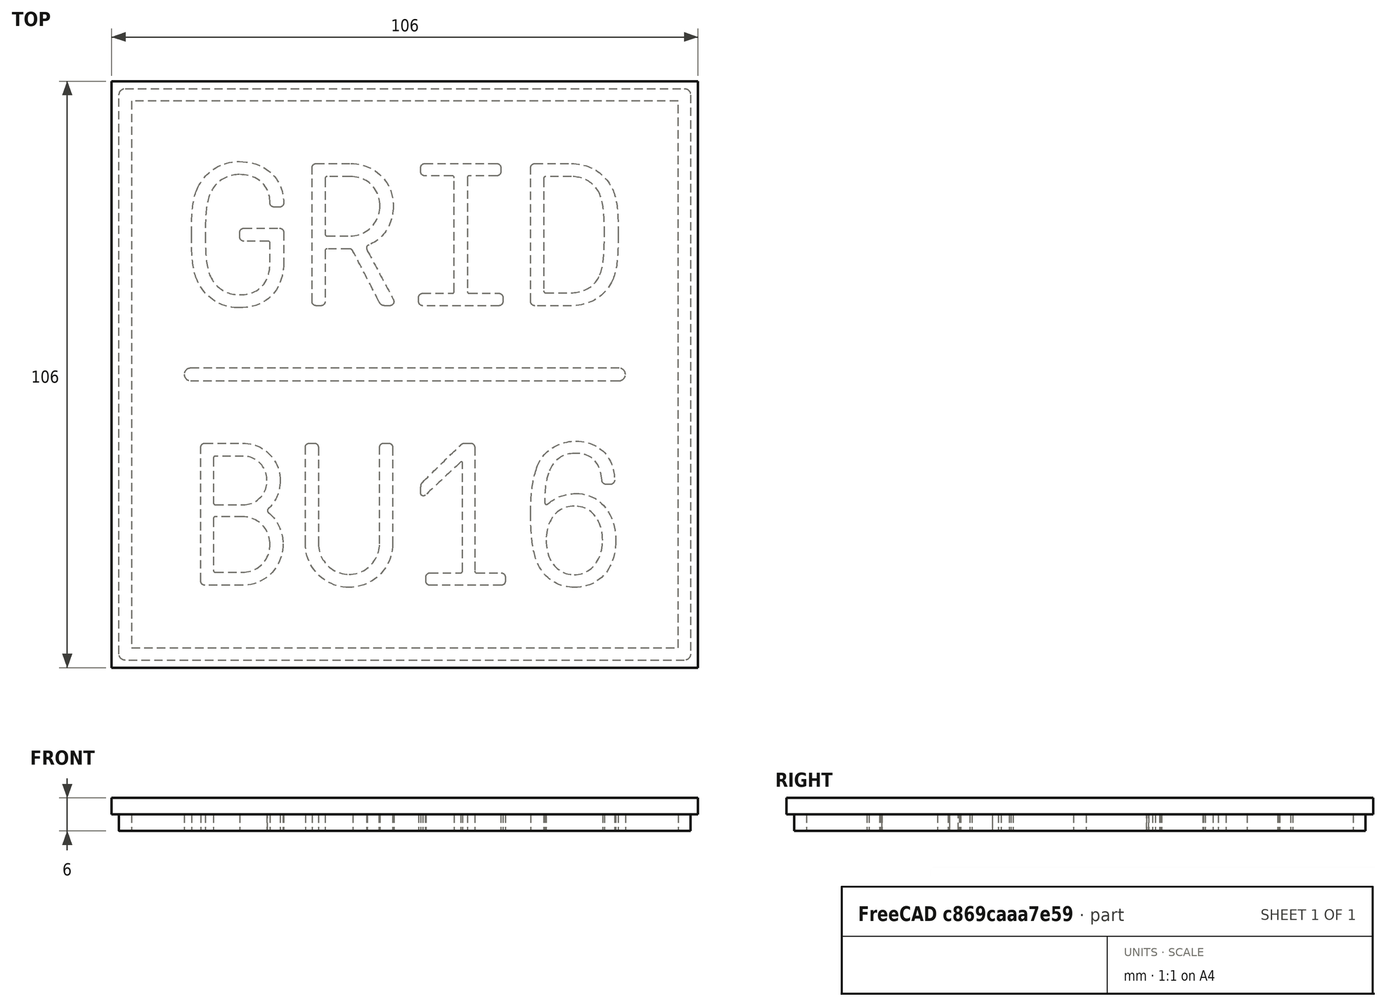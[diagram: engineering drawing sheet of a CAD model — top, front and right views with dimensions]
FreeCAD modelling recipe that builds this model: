
FCSTD DOCUMENT  (FreeCAD 0.18R16131 (Git))
Label: Grid-BU16
License: All rights reserved
LicenseURL: http://en.wikipedia.org/wiki/All_rights_reserved
objects: Sketcher::SketchObject×3, PartDesign::Pad×3, PartDesign::Body×1
note: 10 computed .brp shape members not serialized (recipe doc carries the construction recipe); baked Part::Feature solids carry a one-line shape summary decoded from their .brp

FEATURE [Sketcher::SketchObject] Sketch016
  Placement = pos=(-80,80,0) rot=(0,0,1;0rad)
  sketch-geometry (12):
    g0: BSplineCurve PolesCount=2 KnotsCount=2 Degree=1 IsPeriodic=0
    g1: BSplineCurve PolesCount=4 KnotsCount=2 Degree=3 IsPeriodic=0
    g2: BSplineCurve PolesCount=2 KnotsCount=2 Degree=1 IsPeriodic=0
    g3: BSplineCurve PolesCount=4 KnotsCount=2 Degree=3 IsPeriodic=0
    g4: BSplineCurve PolesCount=2 KnotsCount=2 Degree=1 IsPeriodic=0
    g5: BSplineCurve PolesCount=4 KnotsCount=2 Degree=3 IsPeriodic=0
    g6: BSplineCurve PolesCount=2 KnotsCount=2 Degree=1 IsPeriodic=0
    g7: BSplineCurve PolesCount=4 KnotsCount=2 Degree=3 IsPeriodic=0
    g8: BSplineCurve PolesCount=2 KnotsCount=2 Degree=1 IsPeriodic=0
    g9: BSplineCurve PolesCount=2 KnotsCount=2 Degree=1 IsPeriodic=0
    g10: BSplineCurve PolesCount=2 KnotsCount=2 Degree=1 IsPeriodic=0
    g11: BSplineCurve PolesCount=2 KnotsCount=2 Degree=1 IsPeriodic=0
  constraints (12):
    c: Coincident(g0,g1)
    c: Coincident(g1,g2)
    c: Coincident(g2,g3)
    c: Coincident(g3,g4)
    c: Coincident(g4,g5)
    c: Coincident(g5,g6)
    c: Coincident(g6,g7)
    c: Coincident(g7,g0)
    c: Coincident(g8,g9)
    c: Coincident(g9,g10)
    c: Coincident(g10,g11)
    c: Coincident(g11,g8)
FEATURE [Sketcher::SketchObject] Sketch017
  sketch-geometry (5):
    g0: LineSegment StartX=-53 StartY=53 StartZ=0 EndX=-53 EndY=-53 EndZ=0
    g1: LineSegment StartX=-53 StartY=-53 StartZ=0 EndX=53 EndY=-53 EndZ=0
    g2: LineSegment StartX=53 StartY=-53 StartZ=0 EndX=53 EndY=53 EndZ=0
    g3: LineSegment StartX=53 StartY=53 StartZ=0 EndX=-53 EndY=53 EndZ=0
    g4: Circle [constr] CenterX=0 CenterY=0 CenterZ=0 NormalX=0 NormalY=0 NormalZ=1 AngleXU=0 Radius=74.9533
  constraints (14):
    c: Coincident(g0,g1)
    c: Coincident(g1,g2)
    c: Coincident(g2,g3)
    c: Coincident(g3,g0)
    c: Equal(g0,g1)
    c: Equal(g0,g2)
    c: Equal(g0,g3)
    c: PointOnObject(g0,g4)
    c: PointOnObject(g1,g4)
    c: PointOnObject(g2,g4)
    c: PointOnObject(g3,g4)
    c: Horizontal(g3)
    c: Coincident(g4,g-1)
    c: DistanceX(g3,g3) = 106
FEATURE [PartDesign::Pad] Pad
  Length = 3
  Length2 = 100
  Profile = -> Sketch017
  Type = 0
FEATURE [Sketcher::SketchObject] Sketch018
  Placement = pos=(-80,80,0) rot=(0,0,1;0rad)
  sketch-geometry (178):
    g0: BSplineCurve PolesCount=4 KnotsCount=2 Degree=3 IsPeriodic=0
    g1: BSplineCurve PolesCount=4 KnotsCount=2 Degree=3 IsPeriodic=0
    g2: BSplineCurve PolesCount=4 KnotsCount=2 Degree=3 IsPeriodic=0
    g3: BSplineCurve PolesCount=4 KnotsCount=2 Degree=3 IsPeriodic=0
    g4: BSplineCurve PolesCount=2 KnotsCount=2 Degree=1 IsPeriodic=0
    g5: BSplineCurve PolesCount=4 KnotsCount=2 Degree=3 IsPeriodic=0
    g6: BSplineCurve PolesCount=2 KnotsCount=2 Degree=1 IsPeriodic=0
    g7: BSplineCurve PolesCount=4 KnotsCount=2 Degree=3 IsPeriodic=0
    g8: BSplineCurve PolesCount=4 KnotsCount=2 Degree=3 IsPeriodic=0
    g9: BSplineCurve PolesCount=4 KnotsCount=2 Degree=3 IsPeriodic=0
    g10: BSplineCurve PolesCount=4 KnotsCount=2 Degree=3 IsPeriodic=0
    g11: BSplineCurve PolesCount=2 KnotsCount=2 Degree=1 IsPeriodic=0
    g12: BSplineCurve PolesCount=4 KnotsCount=2 Degree=3 IsPeriodic=0
    g13: BSplineCurve PolesCount=4 KnotsCount=2 Degree=3 IsPeriodic=0
    g14: BSplineCurve PolesCount=2 KnotsCount=2 Degree=1 IsPeriodic=0
    g15: BSplineCurve PolesCount=4 KnotsCount=2 Degree=3 IsPeriodic=0
    g16: BSplineCurve PolesCount=2 KnotsCount=2 Degree=1 IsPeriodic=0
    g17: BSplineCurve PolesCount=4 KnotsCount=2 Degree=3 IsPeriodic=0
    g18: BSplineCurve PolesCount=2 KnotsCount=2 Degree=1 IsPeriodic=0
    g19: BSplineCurve PolesCount=4 KnotsCount=2 Degree=3 IsPeriodic=0
    g20: BSplineCurve PolesCount=2 KnotsCount=2 Degree=1 IsPeriodic=0
    g21: BSplineCurve PolesCount=4 KnotsCount=2 Degree=3 IsPeriodic=0
    g22: BSplineCurve PolesCount=2 KnotsCount=2 Degree=1 IsPeriodic=0
    g23: BSplineCurve PolesCount=4 KnotsCount=2 Degree=3 IsPeriodic=0
    g24: BSplineCurve PolesCount=4 KnotsCount=2 Degree=3 IsPeriodic=0
    g25: BSplineCurve PolesCount=4 KnotsCount=2 Degree=3 IsPeriodic=0
    g26: BSplineCurve PolesCount=4 KnotsCount=2 Degree=3 IsPeriodic=0
    g27: BSplineCurve PolesCount=4 KnotsCount=2 Degree=3 IsPeriodic=0
    g28: BSplineCurve PolesCount=4 KnotsCount=2 Degree=3 IsPeriodic=0
    g29: BSplineCurve PolesCount=2 KnotsCount=2 Degree=1 IsPeriodic=0
    g30: BSplineCurve PolesCount=4 KnotsCount=2 Degree=3 IsPeriodic=0
    g31: BSplineCurve PolesCount=4 KnotsCount=2 Degree=3 IsPeriodic=0
    g32: BSplineCurve PolesCount=4 KnotsCount=2 Degree=3 IsPeriodic=0
    g33: BSplineCurve PolesCount=4 KnotsCount=2 Degree=3 IsPeriodic=0
    g34: BSplineCurve PolesCount=4 KnotsCount=2 Degree=3 IsPeriodic=0
    g35: BSplineCurve PolesCount=4 KnotsCount=2 Degree=3 IsPeriodic=0
    g36: BSplineCurve PolesCount=4 KnotsCount=2 Degree=3 IsPeriodic=0
    g37: BSplineCurve PolesCount=2 KnotsCount=2 Degree=1 IsPeriodic=0
    g38: BSplineCurve PolesCount=4 KnotsCount=2 Degree=3 IsPeriodic=0
    g39: BSplineCurve PolesCount=2 KnotsCount=2 Degree=1 IsPeriodic=0
    g40: BSplineCurve PolesCount=4 KnotsCount=2 Degree=3 IsPeriodic=0
    g41: BSplineCurve PolesCount=2 KnotsCount=2 Degree=1 IsPeriodic=0
    g42: BSplineCurve PolesCount=4 KnotsCount=2 Degree=3 IsPeriodic=0
    g43: BSplineCurve PolesCount=2 KnotsCount=2 Degree=1 IsPeriodic=0
    g44: BSplineCurve PolesCount=4 KnotsCount=2 Degree=3 IsPeriodic=0
    g45: BSplineCurve PolesCount=2 KnotsCount=2 Degree=1 IsPeriodic=0
    g46: BSplineCurve PolesCount=4 KnotsCount=2 Degree=3 IsPeriodic=0
    g47: BSplineCurve PolesCount=4 KnotsCount=2 Degree=3 IsPeriodic=0
    g48: BSplineCurve PolesCount=4 KnotsCount=2 Degree=3 IsPeriodic=0
    g49: BSplineCurve PolesCount=2 KnotsCount=2 Degree=1 IsPeriodic=0
    g50: BSplineCurve PolesCount=4 KnotsCount=2 Degree=3 IsPeriodic=0
    g51: BSplineCurve PolesCount=2 KnotsCount=2 Degree=1 IsPeriodic=0
    g52: BSplineCurve PolesCount=4 KnotsCount=2 Degree=3 IsPeriodic=0
    g53: BSplineCurve PolesCount=2 KnotsCount=2 Degree=1 IsPeriodic=0
    g54: BSplineCurve PolesCount=4 KnotsCount=2 Degree=3 IsPeriodic=0
    g55: BSplineCurve PolesCount=2 KnotsCount=2 Degree=1 IsPeriodic=0
    g56: BSplineCurve PolesCount=4 KnotsCount=2 Degree=3 IsPeriodic=0
    g57: BSplineCurve PolesCount=2 KnotsCount=2 Degree=1 IsPeriodic=0
    g58: BSplineCurve PolesCount=4 KnotsCount=2 Degree=3 IsPeriodic=0
    g59: BSplineCurve PolesCount=2 KnotsCount=2 Degree=1 IsPeriodic=0
    g60: BSplineCurve PolesCount=4 KnotsCount=2 Degree=3 IsPeriodic=0
    g61: BSplineCurve PolesCount=2 KnotsCount=2 Degree=1 IsPeriodic=0
    g62: BSplineCurve PolesCount=4 KnotsCount=2 Degree=3 IsPeriodic=0
    g63: BSplineCurve PolesCount=2 KnotsCount=2 Degree=1 IsPeriodic=0
    g64: BSplineCurve PolesCount=4 KnotsCount=2 Degree=3 IsPeriodic=0
    g65: BSplineCurve PolesCount=2 KnotsCount=2 Degree=1 IsPeriodic=0
    g66: BSplineCurve PolesCount=4 KnotsCount=2 Degree=3 IsPeriodic=0
    g67: BSplineCurve PolesCount=2 KnotsCount=2 Degree=1 IsPeriodic=0
    g68: BSplineCurve PolesCount=4 KnotsCount=2 Degree=3 IsPeriodic=0
    g69: BSplineCurve PolesCount=2 KnotsCount=2 Degree=1 IsPeriodic=0
    g70: BSplineCurve PolesCount=4 KnotsCount=2 Degree=3 IsPeriodic=0
    g71: BSplineCurve PolesCount=2 KnotsCount=2 Degree=1 IsPeriodic=0
    g72: BSplineCurve PolesCount=4 KnotsCount=2 Degree=3 IsPeriodic=0
    g73: BSplineCurve PolesCount=2 KnotsCount=2 Degree=1 IsPeriodic=0
    g74: BSplineCurve PolesCount=4 KnotsCount=2 Degree=3 IsPeriodic=0
    g75: BSplineCurve PolesCount=2 KnotsCount=2 Degree=1 IsPeriodic=0
    g76: BSplineCurve PolesCount=4 KnotsCount=2 Degree=3 IsPeriodic=0
    g77: BSplineCurve PolesCount=2 KnotsCount=2 Degree=1 IsPeriodic=0
    g78: BSplineCurve PolesCount=4 KnotsCount=2 Degree=3 IsPeriodic=0
    g79: BSplineCurve PolesCount=4 KnotsCount=2 Degree=3 IsPeriodic=0
    g80: BSplineCurve PolesCount=4 KnotsCount=2 Degree=3 IsPeriodic=0
    g81: BSplineCurve PolesCount=4 KnotsCount=2 Degree=3 IsPeriodic=0
    g82: BSplineCurve PolesCount=2 KnotsCount=2 Degree=1 IsPeriodic=0
    g83: BSplineCurve PolesCount=4 KnotsCount=2 Degree=3 IsPeriodic=0
    g84: BSplineCurve PolesCount=2 KnotsCount=2 Degree=1 IsPeriodic=0
    g85: BSplineCurve PolesCount=4 KnotsCount=2 Degree=3 IsPeriodic=0
    g86: BSplineCurve PolesCount=2 KnotsCount=2 Degree=1 IsPeriodic=0
    g87: BSplineCurve PolesCount=4 KnotsCount=2 Degree=3 IsPeriodic=0
    g88: BSplineCurve PolesCount=2 KnotsCount=2 Degree=1 IsPeriodic=0
    g89: BSplineCurve PolesCount=4 KnotsCount=2 Degree=3 IsPeriodic=0
    g90: BSplineCurve PolesCount=2 KnotsCount=2 Degree=1 IsPeriodic=0
    g91: BSplineCurve PolesCount=4 KnotsCount=2 Degree=3 IsPeriodic=0
    g92: BSplineCurve PolesCount=4 KnotsCount=2 Degree=3 IsPeriodic=0
    g93: BSplineCurve PolesCount=4 KnotsCount=2 Degree=3 IsPeriodic=0
    g94: BSplineCurve PolesCount=4 KnotsCount=2 Degree=3 IsPeriodic=0
    g95: BSplineCurve PolesCount=2 KnotsCount=2 Degree=1 IsPeriodic=0
    g96: BSplineCurve PolesCount=4 KnotsCount=2 Degree=3 IsPeriodic=0
    g97: BSplineCurve PolesCount=4 KnotsCount=2 Degree=3 IsPeriodic=0
    g98: BSplineCurve PolesCount=2 KnotsCount=2 Degree=1 IsPeriodic=0
    g99: BSplineCurve PolesCount=4 KnotsCount=2 Degree=3 IsPeriodic=0
    g100: BSplineCurve PolesCount=4 KnotsCount=2 Degree=3 IsPeriodic=0
    g101: BSplineCurve PolesCount=2 KnotsCount=2 Degree=1 IsPeriodic=0
    g102: BSplineCurve PolesCount=4 KnotsCount=2 Degree=3 IsPeriodic=0
    g103: BSplineCurve PolesCount=4 KnotsCount=2 Degree=3 IsPeriodic=0
    g104: BSplineCurve PolesCount=2 KnotsCount=2 Degree=1 IsPeriodic=0
    g105: BSplineCurve PolesCount=4 KnotsCount=2 Degree=3 IsPeriodic=0
    g106: BSplineCurve PolesCount=2 KnotsCount=2 Degree=1 IsPeriodic=0
    g107: BSplineCurve PolesCount=4 KnotsCount=2 Degree=3 IsPeriodic=0
    g108: BSplineCurve PolesCount=2 KnotsCount=2 Degree=1 IsPeriodic=0
    g109: BSplineCurve PolesCount=4 KnotsCount=2 Degree=3 IsPeriodic=0
    g110: BSplineCurve PolesCount=2 KnotsCount=2 Degree=1 IsPeriodic=0
    g111: BSplineCurve PolesCount=4 KnotsCount=2 Degree=3 IsPeriodic=0
    g112: BSplineCurve PolesCount=2 KnotsCount=2 Degree=1 IsPeriodic=0
    g113: BSplineCurve PolesCount=4 KnotsCount=2 Degree=3 IsPeriodic=0
    g114: BSplineCurve PolesCount=4 KnotsCount=2 Degree=3 IsPeriodic=0
    g115: BSplineCurve PolesCount=4 KnotsCount=2 Degree=3 IsPeriodic=0
    g116: BSplineCurve PolesCount=4 KnotsCount=2 Degree=3 IsPeriodic=0
    g117: BSplineCurve PolesCount=4 KnotsCount=2 Degree=3 IsPeriodic=0
    g118: BSplineCurve PolesCount=2 KnotsCount=2 Degree=1 IsPeriodic=0
    g119: BSplineCurve PolesCount=4 KnotsCount=2 Degree=3 IsPeriodic=0
    g120: BSplineCurve PolesCount=4 KnotsCount=2 Degree=3 IsPeriodic=0
    g121: BSplineCurve PolesCount=2 KnotsCount=2 Degree=1 IsPeriodic=0
    g122: BSplineCurve PolesCount=4 KnotsCount=2 Degree=3 IsPeriodic=0
    g123: BSplineCurve PolesCount=2 KnotsCount=2 Degree=1 IsPeriodic=0
    g124: BSplineCurve PolesCount=4 KnotsCount=2 Degree=3 IsPeriodic=0
    g125: BSplineCurve PolesCount=2 KnotsCount=2 Degree=1 IsPeriodic=0
    g126: BSplineCurve PolesCount=4 KnotsCount=2 Degree=3 IsPeriodic=0
    g127: BSplineCurve PolesCount=2 KnotsCount=2 Degree=1 IsPeriodic=0
    g128: BSplineCurve PolesCount=4 KnotsCount=2 Degree=3 IsPeriodic=0
    g129: BSplineCurve PolesCount=2 KnotsCount=2 Degree=1 IsPeriodic=0
    g130: BSplineCurve PolesCount=4 KnotsCount=2 Degree=3 IsPeriodic=0
    g131: BSplineCurve PolesCount=2 KnotsCount=2 Degree=1 IsPeriodic=0
    g132: BSplineCurve PolesCount=4 KnotsCount=2 Degree=3 IsPeriodic=0
    g133: BSplineCurve PolesCount=4 KnotsCount=2 Degree=3 IsPeriodic=0
    g134: BSplineCurve PolesCount=2 KnotsCount=2 Degree=1 IsPeriodic=0
    g135: BSplineCurve PolesCount=4 KnotsCount=2 Degree=3 IsPeriodic=0
    g136: BSplineCurve PolesCount=2 KnotsCount=2 Degree=1 IsPeriodic=0
    g137: BSplineCurve PolesCount=4 KnotsCount=2 Degree=3 IsPeriodic=0
    g138: BSplineCurve PolesCount=2 KnotsCount=2 Degree=1 IsPeriodic=0
    g139: BSplineCurve PolesCount=4 KnotsCount=2 Degree=3 IsPeriodic=0
    g140: BSplineCurve PolesCount=4 KnotsCount=2 Degree=3 IsPeriodic=0
    g141: BSplineCurve PolesCount=2 KnotsCount=2 Degree=1 IsPeriodic=0
    g142: BSplineCurve PolesCount=4 KnotsCount=2 Degree=3 IsPeriodic=0
    g143: BSplineCurve PolesCount=2 KnotsCount=2 Degree=1 IsPeriodic=0
    g144: BSplineCurve PolesCount=4 KnotsCount=2 Degree=3 IsPeriodic=0
    g145: BSplineCurve PolesCount=2 KnotsCount=2 Degree=1 IsPeriodic=0
    g146: BSplineCurve PolesCount=4 KnotsCount=2 Degree=3 IsPeriodic=0
    g147: BSplineCurve PolesCount=2 KnotsCount=2 Degree=1 IsPeriodic=0
    g148: BSplineCurve PolesCount=4 KnotsCount=2 Degree=3 IsPeriodic=0
    g149: BSplineCurve PolesCount=2 KnotsCount=2 Degree=1 IsPeriodic=0
    g150: BSplineCurve PolesCount=4 KnotsCount=2 Degree=3 IsPeriodic=0
    g151: BSplineCurve PolesCount=2 KnotsCount=2 Degree=1 IsPeriodic=0
    g152: BSplineCurve PolesCount=4 KnotsCount=2 Degree=3 IsPeriodic=0
    g153: BSplineCurve PolesCount=2 KnotsCount=2 Degree=1 IsPeriodic=0
    g154: BSplineCurve PolesCount=4 KnotsCount=2 Degree=3 IsPeriodic=0
    g155: BSplineCurve PolesCount=2 KnotsCount=2 Degree=1 IsPeriodic=0
    g156: BSplineCurve PolesCount=4 KnotsCount=2 Degree=3 IsPeriodic=0
    g157: BSplineCurve PolesCount=2 KnotsCount=2 Degree=1 IsPeriodic=0
    g158: BSplineCurve PolesCount=4 KnotsCount=2 Degree=3 IsPeriodic=0
    g159: BSplineCurve PolesCount=2 KnotsCount=2 Degree=1 IsPeriodic=0
    g160: BSplineCurve PolesCount=4 KnotsCount=2 Degree=3 IsPeriodic=0
    g161: BSplineCurve PolesCount=2 KnotsCount=2 Degree=1 IsPeriodic=0
    g162: BSplineCurve PolesCount=4 KnotsCount=2 Degree=3 IsPeriodic=0
    g163: BSplineCurve PolesCount=4 KnotsCount=2 Degree=3 IsPeriodic=0
    g164: BSplineCurve PolesCount=4 KnotsCount=2 Degree=3 IsPeriodic=0
    g165: BSplineCurve PolesCount=4 KnotsCount=2 Degree=3 IsPeriodic=0
    g166: BSplineCurve PolesCount=4 KnotsCount=2 Degree=3 IsPeriodic=0
    g167: BSplineCurve PolesCount=4 KnotsCount=2 Degree=3 IsPeriodic=0
    g168: BSplineCurve PolesCount=2 KnotsCount=2 Degree=1 IsPeriodic=0
    g169: BSplineCurve PolesCount=4 KnotsCount=2 Degree=3 IsPeriodic=0
    g170: BSplineCurve PolesCount=4 KnotsCount=2 Degree=3 IsPeriodic=0
    g171: BSplineCurve PolesCount=4 KnotsCount=2 Degree=3 IsPeriodic=0
    g172: BSplineCurve PolesCount=4 KnotsCount=2 Degree=3 IsPeriodic=0
    g173: BSplineCurve PolesCount=4 KnotsCount=2 Degree=3 IsPeriodic=0
    g174: BSplineCurve PolesCount=4 KnotsCount=2 Degree=3 IsPeriodic=0
    g175: BSplineCurve PolesCount=4 KnotsCount=2 Degree=3 IsPeriodic=0
    g176: BSplineCurve PolesCount=4 KnotsCount=2 Degree=3 IsPeriodic=0
    g177: BSplineCurve PolesCount=4 KnotsCount=2 Degree=3 IsPeriodic=0
  constraints (178):
    c: Coincident(g0,g1)
    c: Coincident(g1,g2)
    c: Coincident(g2,g3)
    c: Coincident(g3,g0)
    c: Coincident(g4,g5)
    c: Coincident(g5,g6)
    c: Coincident(g6,g7)
    c: Coincident(g7,g8)
    c: Coincident(g8,g9)
    c: Coincident(g9,g10)
    c: Coincident(g10,g11)
    c: Coincident(g11,g12)
    c: Coincident(g12,g13)
    c: Coincident(g13,g14)
    c: Coincident(g14,g15)
    c: Coincident(g15,g16)
    c: Coincident(g16,g17)
    c: Coincident(g17,g18)
    c: Coincident(g18,g19)
    c: Coincident(g19,g20)
    c: Coincident(g20,g21)
    c: Coincident(g21,g22)
    c: Coincident(g22,g23)
    c: Coincident(g23,g4)
    c: Coincident(g24,g25)
    c: Coincident(g25,g26)
    c: Coincident(g26,g27)
    c: Coincident(g27,g28)
    c: Coincident(g28,g29)
    c: Coincident(g29,g30)
    c: Coincident(g30,g31)
    c: Coincident(g31,g32)
    c: Coincident(g32,g33)
    c: Coincident(g33,g34)
    c: Coincident(g34,g35)
    c: Coincident(g35,g36)
    c: Coincident(g36,g37)
    c: Coincident(g37,g38)
    c: Coincident(g38,g39)
    c: Coincident(g39,g40)
    c: Coincident(g40,g41)
    c: Coincident(g41,g42)
    c: Coincident(g42,g43)
    c: Coincident(g43,g44)
    c: Coincident(g44,g45)
    c: Coincident(g45,g46)
    c: Coincident(g46,g47)
    c: Coincident(g47,g24)
    c: Coincident(g48,g49)
    c: Coincident(g49,g50)
    c: Coincident(g50,g51)
    c: Coincident(g51,g52)
    c: Coincident(g52,g53)
    c: Coincident(g53,g54)
    c: Coincident(g54,g48)
    c: Coincident(g55,g56)
    c: Coincident(g56,g57)
    c: Coincident(g57,g58)
    c: Coincident(g58,g59)
    c: Coincident(g59,g60)
    c: Coincident(g60,g61)
    c: Coincident(g61,g62)
    c: Coincident(g62,g63)
    c: Coincident(g63,g64)
    c: Coincident(g64,g65)
    c: Coincident(g65,g66)
    c: Coincident(g66,g67)
    c: Coincident(g67,g68)
    c: Coincident(g68,g69)
    c: Coincident(g69,g70)
    c: Coincident(g70,g71)
    c: Coincident(g71,g72)
    c: Coincident(g72,g73)
    c: Coincident(g73,g74)
    c: Coincident(g74,g75)
    c: Coincident(g75,g76)
    c: Coincident(g76,g77)
    c: Coincident(g77,g78)
    c: Coincident(g78,g55)
    c: Coincident(g79,g80)
    c: Coincident(g80,g81)
    c: Coincident(g81,g82)
    c: Coincident(g82,g83)
    c: Coincident(g83,g84)
    c: Coincident(g84,g85)
    c: Coincident(g85,g86)
    c: Coincident(g86,g87)
    c: Coincident(g87,g79)
    c: Coincident(g88,g89)
    c: Coincident(g89,g90)
    c: Coincident(g90,g91)
    c: Coincident(g91,g92)
    c: Coincident(g92,g93)
    c: Coincident(g93,g94)
    c: Coincident(g94,g95)
    c: Coincident(g95,g96)
    c: Coincident(g96,g88)
    c: Coincident(g97,g98)
    c: Coincident(g98,g99)
    c: Coincident(g99,g100)
    c: Coincident(g100,g101)
    c: Coincident(g101,g102)
    c: Coincident(g102,g97)
    c: Coincident(g103,g104)
    c: Coincident(g104,g105)
    c: Coincident(g105,g106)
    c: Coincident(g106,g107)
    c: Coincident(g107,g108)
    c: Coincident(g108,g109)
    c: Coincident(g109,g103)
    c: Coincident(g110,g111)
    c: Coincident(g111,g112)
    c: Coincident(g112,g113)
    c: Coincident(g113,g114)
    c: Coincident(g114,g115)
    c: Coincident(g115,g116)
    c: Coincident(g116,g117)
    c: Coincident(g117,g118)
    c: Coincident(g118,g119)
    c: Coincident(g119,g110)
    c: Coincident(g120,g121)
    c: Coincident(g121,g122)
    c: Coincident(g122,g123)
    c: Coincident(g123,g124)
    c: Coincident(g124,g125)
    c: Coincident(g125,g126)
    c: Coincident(g126,g120)
    c: Coincident(g127,g128)
    c: Coincident(g128,g129)
    c: Coincident(g129,g130)
    c: Coincident(g130,g131)
    c: Coincident(g131,g132)
    c: Coincident(g132,g133)
    c: Coincident(g133,g134)
    c: Coincident(g134,g135)
    c: Coincident(g135,g136)
    c: Coincident(g136,g137)
    c: Coincident(g137,g138)
    c: Coincident(g138,g139)
    c: Coincident(g139,g140)
    c: Coincident(g140,g127)
    c: Coincident(g141,g142)
    c: Coincident(g142,g143)
    c: Coincident(g143,g144)
    c: Coincident(g144,g145)
    c: Coincident(g145,g146)
    c: Coincident(g146,g147)
    c: Coincident(g147,g148)
    c: Coincident(g148,g149)
    c: Coincident(g149,g150)
    c: Coincident(g150,g151)
    c: Coincident(g151,g152)
    c: Coincident(g152,g153)
    c: Coincident(g153,g154)
    c: Coincident(g154,g155)
    c: Coincident(g155,g156)
    c: Coincident(g156,g157)
    c: Coincident(g157,g158)
    c: Coincident(g158,g159)
    c: Coincident(g159,g160)
    c: Coincident(g160,g161)
    c: Coincident(g161,g162)
    c: Coincident(g162,g141)
    c: Coincident(g163,g164)
    c: Coincident(g164,g165)
    c: Coincident(g165,g166)
    c: Coincident(g166,g167)
    c: Coincident(g167,g168)
    c: Coincident(g168,g169)
    c: Coincident(g169,g170)
    c: Coincident(g170,g171)
    c: Coincident(g171,g172)
    c: Coincident(g172,g173)
    c: Coincident(g173,g174)
    c: Coincident(g174,g175)
    c: Coincident(g175,g176)
    c: Coincident(g176,g177)
    c: Coincident(g177,g163)
FEATURE [PartDesign::Pad] Pad001
  BaseFeature = -> Pad
  Length = 3
  Length2 = 100
  Profile = -> Sketch016
  Reversed = true
  Type = 0
FEATURE [PartDesign::Pad] Pad002
  BaseFeature = -> Pad001
  Length = 3
  Length2 = 100
  Profile = -> Sketch018
  Reversed = true
  Type = 0
FEATURE [PartDesign::Body] Body
  Group = -> [Sketch016,Sketch017,Pad,Sketch018,Pad001,Pad002]
  Origin = -> Origin
  Tip = -> Pad002
